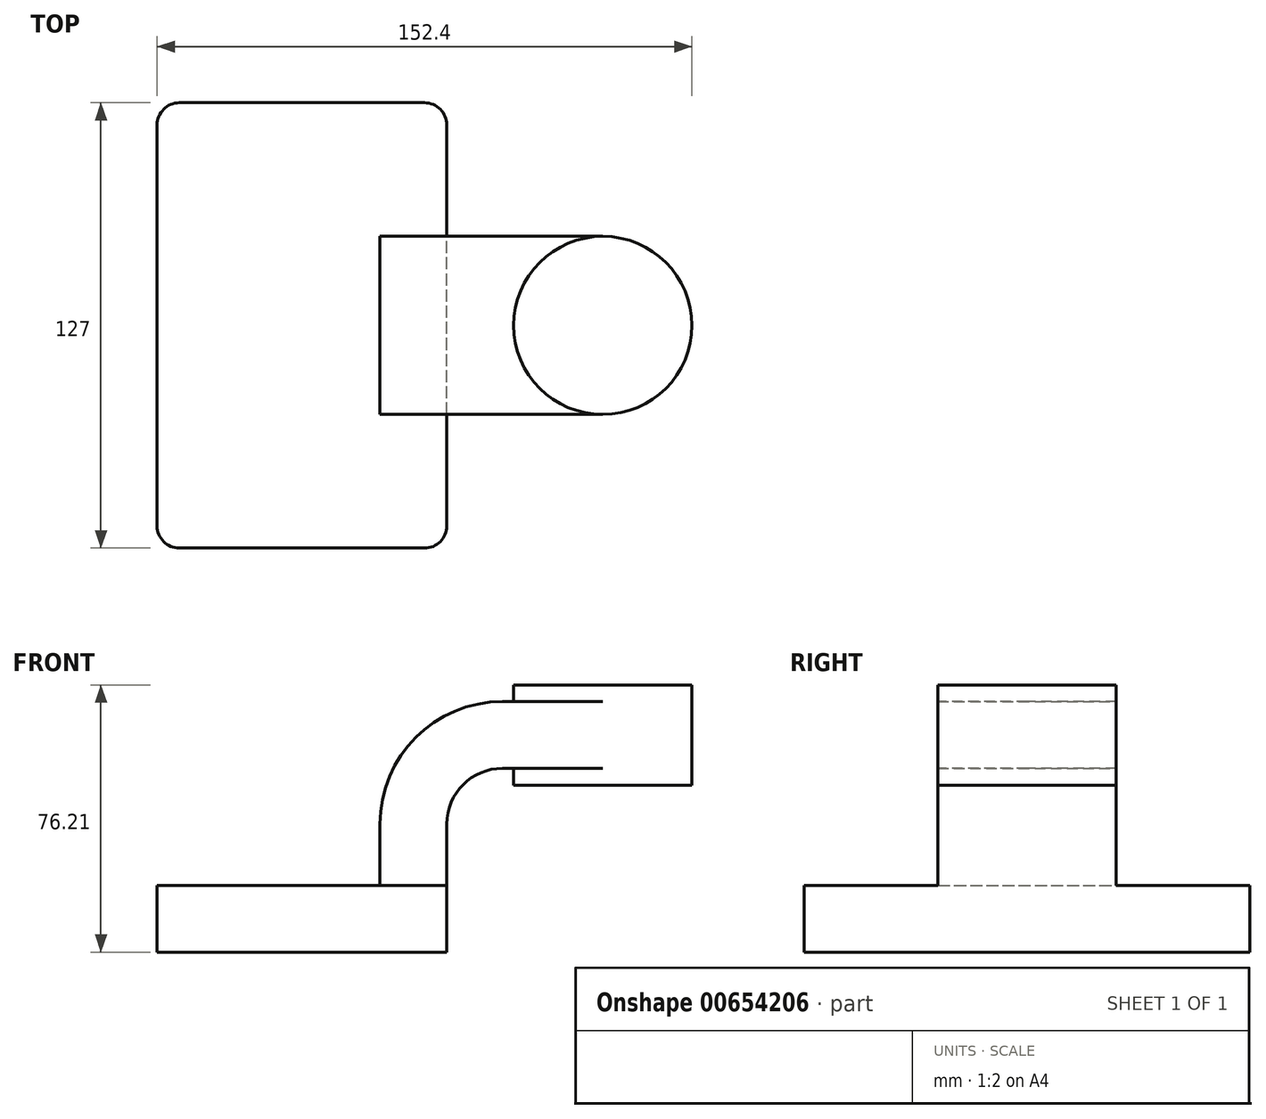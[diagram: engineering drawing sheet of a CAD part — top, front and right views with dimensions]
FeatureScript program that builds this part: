
annotation { "Feature Type Name" : "Feature", "Feature Type Description" : "" }
export const myFeature = defineFeature(function(context is Context, id is Id, definition is map)
    precondition{}
    {
        {
            var Q0;
            Q0=qCreatedBy(makeId("Front.planeOp"),FACE);
            var sketch = newSketch(context, id + "F0", { "sketchPlane" : qUnion([Q0])});
            skLineSegment(sketch, "E0.bottom", {"start": v(-41.28, -9.53) * mm, "end": v(41.28, -9.53) * mm});
            skLineSegment(sketch, "E0.top", {"start": v(-41.28, 9.52) * mm, "end": v(41.28, 9.52) * mm});
            skLineSegment(sketch, "E0.left", {"start": v(-41.28, -9.53) * mm, "end": v(-41.28, 9.53) * mm});
            skLineSegment(sketch, "E0.right", {"start": v(41.28, -9.53) * mm, "end": v(41.28, 9.52) * mm});
            skPoint(sketch, "E0.middle", {"position": v(0, 0) * mm});
            skLineSegment(sketch, "E1.bottom", {"start": v(60.33, 38.1) * mm, "end": v(111.12, 38.1) * mm});
            skLineSegment(sketch, "E1.top", {"start": v(60.33, 66.67) * mm, "end": v(111.12, 66.67) * mm});
            skLineSegment(sketch, "E1.left", {"start": v(60.33, 38.1) * mm, "end": v(60.33, 66.67) * mm});
            skLineSegment(sketch, "E1.right", {"start": v(111.12, 38.1) * mm, "end": v(111.12, 66.67) * mm});
            skPoint(sketch, "E1.middle", {"position": v(85.72, 52.39) * mm});
            skLineSegment(sketch, "E2", {"start": v(41.28, 9.52) * mm, "end": v(41.28, 27) * mm});
            skArc(sketch, "E3", {"start": v(41.27, 27) * mm, "mid": v(45.92, 38.23) * mm, "end": v(57.15, 42.88) * mm});
            skLineSegment(sketch, "E4", {"start": v(57.15, 42.88) * mm, "end": v(94.7, 42.88) * mm});
            skLineSegment(sketch, "E5.0", {"start": v(57.15, 61.93) * mm, "end": v(94.7, 61.93) * mm});
            skArc(sketch, "E5.1", {"start": v(22.22, 27) * mm, "mid": v(32.45, 51.7) * mm, "end": v(57.15, 61.93) * mm});
            skLineSegment(sketch, "E5.2", {"start": v(22.22, 9.52) * mm, "end": v(22.22, 27) * mm});
            skLineSegment(sketch, "E6", {"start": v(85.72, 38.1) * mm, "end": v(85.72, 66.67) * mm});
            skFitSpline(sketch, "E7", {"points": [v(-41.28, 9.52) * mm, v(57.15, 61.93) * mm], "startDerivative": vector(-4.58, 109.23) * mm, "endDerivative": vector(107.97, -28.79) * mm});
            skSolve(sketch);
        }
        {
            var Q0;
            Q0=makeQuery(id+"F0.imprint","IMPRINT",FACE,{"disambiguationData":[TD([[makeQuery(id+"F0.imprint","IMPRINT",EDGE,{"derivedFrom":sQuery(id+"F0.wireOp",EDGE,"E0.bottom")}),1.0]])]});
            extrude(context, id + "F1", {"entities" : qUnion([Q0]), "endBound" : BoundingType.SYMMETRIC, "depth" : 127 * mm, "offsetDistance" : 25.4 * mm});
        }
        {
            var Q0;
            {var subQ1=sQuery(id+"F0.wireOp",EDGE,"E2");Q0=makeQuery(id+"F0.imprint","IMPRINT",FACE,{"disambiguationData":[TD([[makeQuery(id+"F0.imprint","IMPRINT",EDGE,{"derivedFrom":subQ1}),1.0]])]});}
            extrude(context, id + "F2", {"entities" : qUnion([Q0]), "operationType" : NewBodyOperationType.ADD, "endBound" : BoundingType.SYMMETRIC, "depth" : 50.8 * mm, "offsetDistance" : 25.4 * mm});
        }
        {
            var Q0;
            {var subQ0=sQuery(id+"F0.wireOp",EDGE,"E4");var subQ1=sQuery(id+"F0.wireOp",EDGE,"E1.left");var subQ2=makeQuery(id+"F0.imprint","INTERSECT",VERTEX,{"derivedFrom":[subQ1,subQ0]});Q0=makeQuery(id+"F0.imprint","IMPRINT",FACE,{"disambiguationData":[TD([[makeQuery(id+"F0.imprint","IMPRINT",EDGE,{"disambiguationData":[TD([[subQ2,-1.0]])],"derivedFrom":subQ1}),-1.0]])]});}
            extrude(context, id + "F3", {"entities" : qUnion([Q0]), "operationType" : NewBodyOperationType.ADD, "endBound" : BoundingType.SYMMETRIC, "depth" : 50.8 * mm, "offsetDistance" : 25.4 * mm});
        }
        {
            var Q0;
            Q0=makeQuery(id+"F0.imprint","IMPRINT",FACE,{"disambiguationData":[TD([[makeQuery(id+"F0.imprint","IMPRINT",EDGE,{"derivedFrom":sQuery(id+"F0.wireOp",EDGE,"E5.1")}),1.0]])]});
            extrude(context, id + "F4", {"entities" : qUnion([Q0]), "operationType" : NewBodyOperationType.ADD, "endBound" : BoundingType.SYMMETRIC, "depth" : 15.88 * mm, "offsetDistance" : 25.4 * mm});
        }
        {
            var Q0;
            {var subQ0=sQuery(id+"F0.wireOp",EDGE,"E1.right");Q0=makeQuery(id+"F0.imprint","IMPRINT",FACE,{"disambiguationData":[TD([[makeQuery(id+"F0.imprint","IMPRINT",EDGE,{"derivedFrom":subQ0}),1.0]])]});}
            var Q1;
            Q1=sQuery(id+"F0.wireOp",EDGE,"E6");
            revolve(context, id + "F5", {"operationType" : NewBodyOperationType.ADD, "entities" : qUnion([Q0]), "axis" : qUnion([Q1]), "revolveType" : RevolveType.FULL});
        }
        {
            var Q0;
            Q0=makeQuery(id+"F1.opExtrude","CAP_EDGE",EDGE,{"disambiguationData":[OSD([sQuery(id+"F0.wireOp",EDGE,"E0.right")])],"isStart":false});
            var Q1;
            Q1=makeQuery(id+"F1.opExtrude","CAP_EDGE",EDGE,{"disambiguationData":[OSD([sQuery(id+"F0.wireOp",EDGE,"E0.left")])],"isStart":false});
            var Q2;
            Q2=makeQuery(id+"F1.opExtrude","CAP_EDGE",EDGE,{"disambiguationData":[OSD([sQuery(id+"F0.wireOp",EDGE,"E0.right")])],"isStart":true});
            var Q3;
            Q3=makeQuery(id+"F1.opExtrude","CAP_EDGE",EDGE,{"disambiguationData":[OSD([sQuery(id+"F0.wireOp",EDGE,"E0.left")])],"isStart":true});
            fillet(context, id + "F6", {"entities" : qUnion([Q0, Q1, Q2, Q3]), "radius" : 6.35 * mm, "tangentPropagation" : true, "allowEdgeOverflow" : false});
        }
    });
